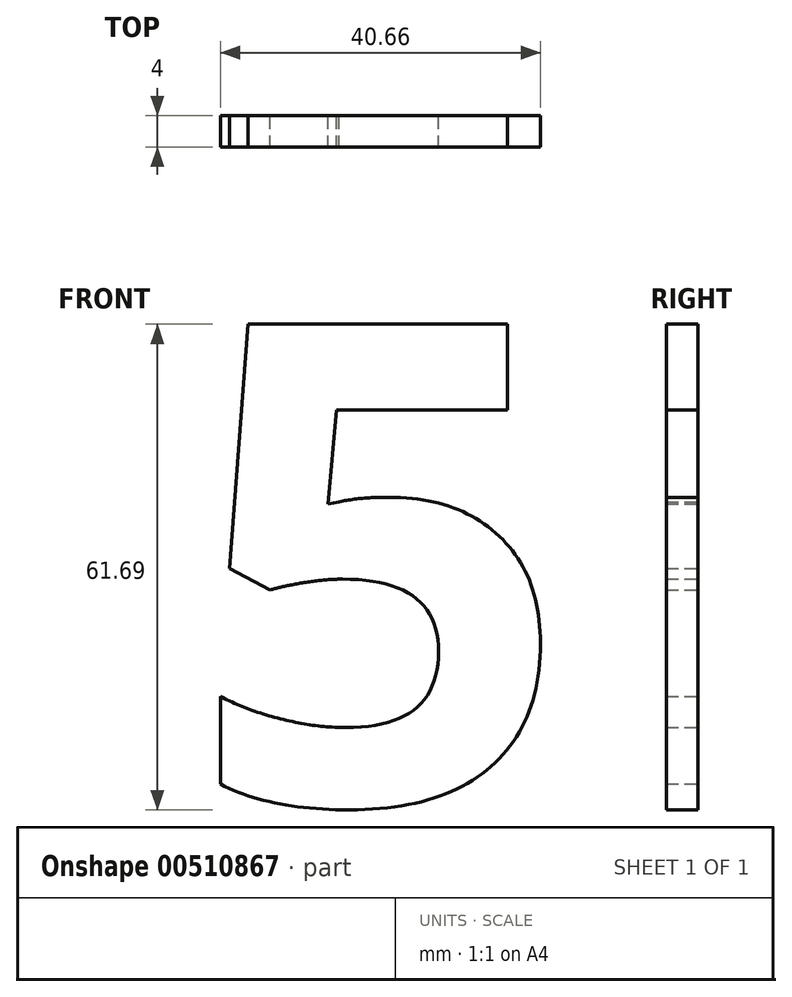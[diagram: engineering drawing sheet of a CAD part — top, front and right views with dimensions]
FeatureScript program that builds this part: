
annotation { "Feature Type Name" : "Feature", "Feature Type Description" : "" }
export const myFeature = defineFeature(function(context is Context, id is Id, definition is map)
    precondition{}
    {
        {
            var Q0;
            Q0=qCreatedBy(makeId("Front.planeOp"),FACE);
            var sketch = newSketch(context, id + "F0", { "sketchPlane" : qUnion([Q0])});
            skText(sketch, "E0", { "text": "5", "fontName": "OpenSans-Bold.ttf"});
            const initialGuessF0  = {"E0": [0, 0, 1, 0, 0.06137]};
            skSetInitialGuess(sketch, initialGuessF0);
            skSolve(sketch);
        }
        {
            var Q0;
            Q0=makeQuery(id+"F0.imprint","IMPRINT",FACE,{"disambiguationData":[TD([[makeQuery(id+"F0.imprint","IMPRINT",EDGE,{"derivedFrom":sQuery(id+"F0.wireOp",EDGE,"E0.sketch_text.stroke-0")}),-1.0]])]});
            extrude(context, id + "F1", {"entities" : qUnion([Q0]), "depth" : 4 * mm});
        }
    });
